# Revit family: Legrand Marina horizontal version references 036911 to 036981
name_source: partatom
category: Installations électriques
revit_build: Autodesk Revit 2018 (Build: 20170223_1515(x64)
units: mm (PartAtom-declared; Revit-internal decimal feet)

## family parameters
Basée sur le plan de construction = Non
Conserver l'orientation des annotations = Non
Cote de connecteur circulaire = Utiliser le diamètre
Couper avec des vides une fois chargée = Non
Numéro OmniClass = 23.80.00.00
Partagée = Non
Point de calcul de pièce = Non
Titre OmniClass = Electric Power and Lighting
Toujours verticalement = Oui
Type d'élément = Normal

## types (8) — shared parameters
ETIM Class = EC000058
Fabricant = Legrand
General Conditions of Use = https://export.legrand.com
Glass door = Non
Horizontal version = Oui
IK = 10
Material = Metallic
RAL = 7035
Square version = Non
URL = www.legrand.fr
Vertical version = Non

## per-type parameters (varying)
| type | Cabinet 036911 | Cabinet 036975 | Cabinet 036976 | Cabinet 036977 | Cabinet 036978 | Cabinet 036979 | Cabinet 036980 | Cabinet 036981 | IP | Length | Number of door | depth | height | weight |
| Legrand Atlantic 036911 | Oui | Non | Non | Non | Non | Non | Non | Non | 66 | 400 mm  [stored 1.31234 ft] | 1 | 160 mm  [stored 0.524934 ft] | 300 mm | 6.20 kg |
| Legrand Atlantic 036976 | Non | Non | Oui | Non | Non | Non | Non | Non | 66 | 600 mm | 1 | 200 mm  [stored 0.656168 ft] | 400 mm  [stored 1.31234 ft] | 14.80 kg |
| Legrand Atlantic 036975 | Non | Oui | Non | Non | Non | Non | Non | Non | 66 | 400 mm  [stored 1.31234 ft] | 1 | 200 mm  [stored 0.656168 ft] | 300 mm | 14.10 kg |
| Legrand Atlantic 036977 | Non | Non | Non | Oui | Non | Non | Non | Non | 66 | 600 mm | 1 | 250 mm  [stored 0.82021 ft] | 400 mm  [stored 1.31234 ft] | 13.30 kg |
| Legrand Atlantic 036978 | Non | Non | Non | Non | Oui | Non | Non | Non | 55 | 800 mm  [stored 2.62467 ft] | 2 | 300 mm | 600 mm | 32.60 kg |
| Legrand Atlantic 036979 | Non | Non | Non | Non | Non | Oui | Non | Non | 55 | 1000 mm  [stored 3.28084 ft] | 2 | 300 mm | 600 mm | 32.60 kg |
| Legrand Atlantic 036980 | Non | Non | Non | Non | Non | Non | Oui | Non | 55 | 1000 mm  [stored 3.28084 ft] | 2 | 300 mm | 800 mm  [stored 2.62467 ft] | 53.60 kg |
| Legrand Atlantic 036981 | Non | Non | Non | Non | Non | Non | Non | Oui | 55 | 1200 mm | 2 | 300 mm | 1000 mm  [stored 3.28084 ft] | 80.60 kg |

note: column(s) folded — value = type name in every type: Description

note: [stored X ft] marks values corroborated as IEEE doubles in the binary element streams (Revit-internal decimal feet)
